# Revit family: S-775
name_source: partatom
category: Plumbing Fixtures
revit_build: Autodesk Revit 2015 (Build: 20140606_1530(x64)
units: mm (PartAtom-declared; Revit-internal decimal feet)

## types (6) — shared parameters
B = 72 mm
Description = CHANNEL GRID, WAVES, FOR CHANNELS WIDTH 70
Grid = INOX AISI304
Manufacturer = Jimten
Material = INOX AISI304
Model = S-775
Type Comments = COMPATIBLE WITH VISIBLE OR THIN FRAMES
URL = http://www.jimten.com

## per-type parameters (varying)
| type | A | DistExt | N_MatrizHuecos | Reference | Size |
| 70x350mm_WAVES | 340 mm | 45 mm | 2 | 13738 | 350mm x 70mm |
| 70x550mm_WAVES | 540 mm  [stored 1.77165 ft] | 20 mm  [stored 0.0656168 ft] | 4 | 13758 | 550mm x 70mm |
| 70x650mm_WAVES | 640 mm  [stored 2.09974 ft] | 70 mm | 4 | 13768 | 650mm x 70mm |
| 70x750mm_WAVES | 740 mm | 55 mm | 5 | 13778 | 750mm x 70mm |
| 70x850mm_WAVES | 840 mm | 40 mm | 6 | 13788 | 850mm x 70mm |
| 70x950mm_WAVES | 940 mm | 30 mm  [stored 0.0984252 ft] | 7 | 13798 | 950mm x 70mm |

note: [stored X ft] marks values corroborated as IEEE doubles in the binary element streams (Revit-internal decimal feet)

## geometry (parser evidence)
native form markers: Blend x3, Sweep x2
no freeform markers — native parametric forms only
